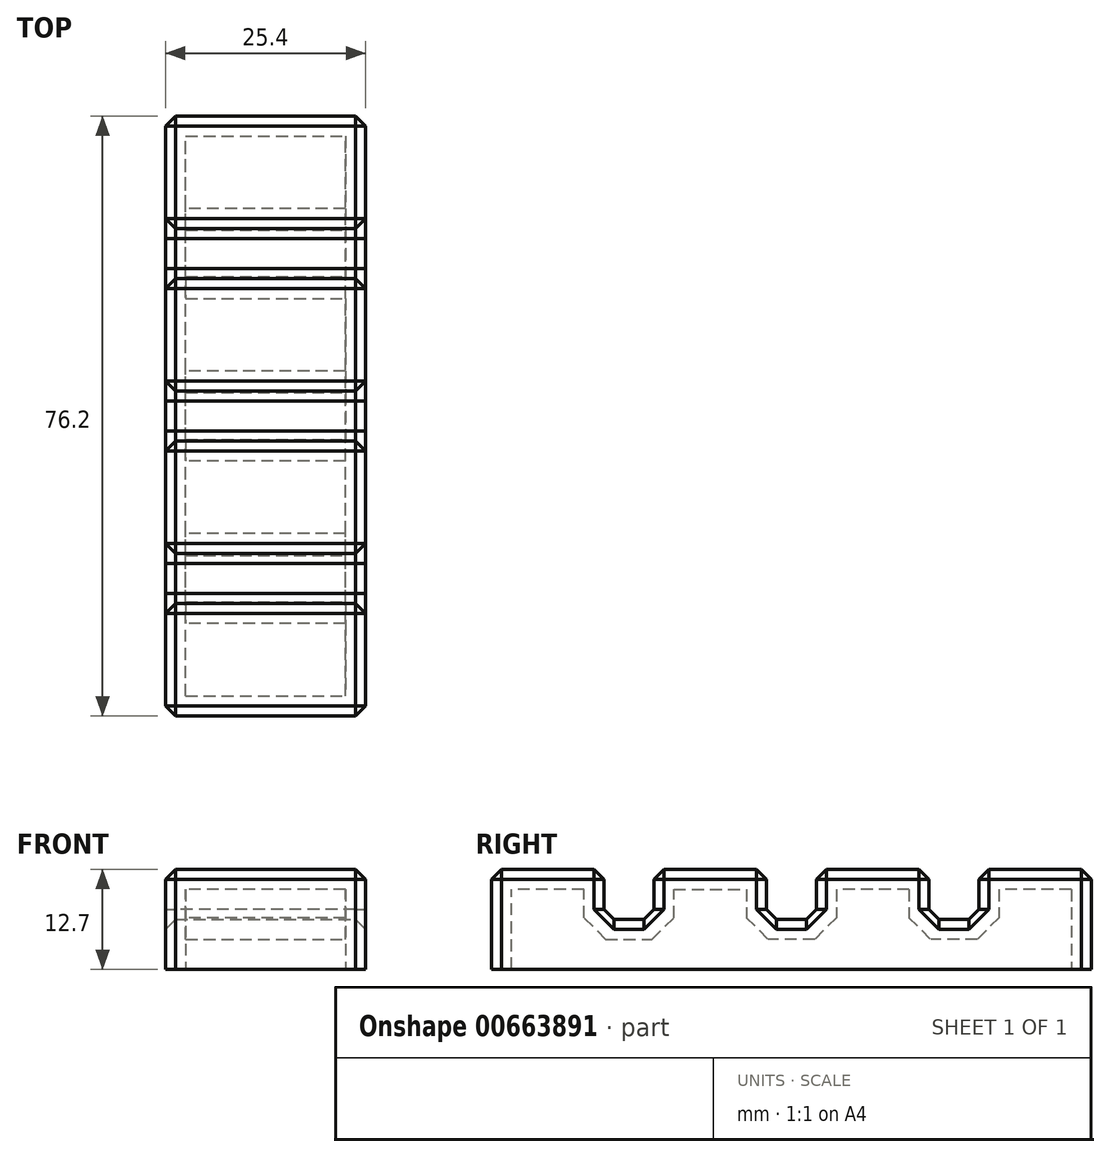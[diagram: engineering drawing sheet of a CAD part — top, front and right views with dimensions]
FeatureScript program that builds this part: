
annotation { "Feature Type Name" : "Feature", "Feature Type Description" : "" }
export const myFeature = defineFeature(function(context is Context, id is Id, definition is map)
    precondition{}
    {
        {
            var Q0;
            Q0=qCreatedBy(makeId("Top.planeOp"),FACE);
            var sketch = newSketch(context, id + "F0", { "sketchPlane" : qUnion([Q0])});
            skLineSegment(sketch, "E0.bottom", {"start": v(-12.7, -38.1) * mm, "end": v(12.7, -38.1) * mm});
            skLineSegment(sketch, "E0.top", {"start": v(-12.7, 38.1) * mm, "end": v(12.7, 38.1) * mm});
            skLineSegment(sketch, "E0.left", {"start": v(-12.7, -38.1) * mm, "end": v(-12.7, 38.1) * mm});
            skLineSegment(sketch, "E0.right", {"start": v(12.7, -38.1) * mm, "end": v(12.7, 38.1) * mm});
            skPoint(sketch, "E0.middle", {"position": v(0, 0) * mm});
            skSolve(sketch);
        }
        {
            var Q0;
            Q0 = qSketchRegion(id + "F0", true);
            extrude(context, id + "F1", {"entities" : qUnion([Q0]), "depth" : 12.7 * mm, "offsetDistance" : 25.4 * mm});
        }
        {
            var Q0;
            Q0=makeQuery(id+"F1.opExtrude","SWEPT_FACE",FACE,{"disambiguationData":[OSD([sQuery(id+"F0.wireOp",EDGE,"E0.left")])]});
            var sketch = newSketch(context, id + "F2", { "sketchPlane" : qUnion([Q0])});
            skLineSegment(sketch, "E1", {"start": v(-38.1, 6.35) * mm, "end": v(38.1, 6.35) * mm, "construction": true});
            skLineSegment(sketch, "E2.bottom", {"start": v(3.18, 6.35) * mm, "end": v(-3.17, 6.35) * mm});
            skLineSegment(sketch, "E2.top", {"start": v(3.18, 19.05) * mm, "end": v(-3.17, 19.05) * mm});
            skLineSegment(sketch, "E2.left", {"start": v(3.18, 6.35) * mm, "end": v(3.18, 19.05) * mm});
            skLineSegment(sketch, "E2.right", {"start": v(-3.17, 6.35) * mm, "end": v(-3.17, 19.05) * mm});
            skPoint(sketch, "E2.middle", {"position": v(0, 12.7) * mm});
            skLineSegment(sketch, "E3.bottom", {"start": v(23.83, 6.35) * mm, "end": v(17.48, 6.35) * mm});
            skLineSegment(sketch, "E3.top", {"start": v(23.83, 19.05) * mm, "end": v(17.48, 19.05) * mm});
            skLineSegment(sketch, "E3.left", {"start": v(23.83, 6.35) * mm, "end": v(23.83, 19.05) * mm});
            skLineSegment(sketch, "E3.right", {"start": v(17.48, 6.35) * mm, "end": v(17.48, 19.05) * mm});
            skPoint(sketch, "E3.middle", {"position": v(20.65, 12.7) * mm});
            skLineSegment(sketch, "E4.bottom", {"start": v(-17.48, 6.35) * mm, "end": v(-23.83, 6.35) * mm});
            skLineSegment(sketch, "E4.top", {"start": v(-17.48, 19.05) * mm, "end": v(-23.83, 19.05) * mm});
            skLineSegment(sketch, "E4.left", {"start": v(-17.48, 6.35) * mm, "end": v(-17.48, 19.05) * mm});
            skLineSegment(sketch, "E4.right", {"start": v(-23.83, 6.35) * mm, "end": v(-23.83, 19.05) * mm});
            skPoint(sketch, "E4.middle", {"position": v(-20.65, 12.7) * mm});
            skSolve(sketch);
        }
        {
            var Q0;
            {var subQ0=sQuery(id+"F2.wireOp",EDGE,"E4.bottom");Q0=makeQuery(id+"F2.imprint","IMPRINT",FACE,{"disambiguationData":[TD([[makeQuery(id+"F2.imprint","IMPRINT",EDGE,{"derivedFrom":subQ0}),-1.0]])]});}
            var Q1;
            {var subQ0=sQuery(id+"F2.wireOp",EDGE,"E4.top");Q1=makeQuery(id+"F2.imprint","IMPRINT",FACE,{"disambiguationData":[TD([[makeQuery(id+"F2.imprint","IMPRINT",EDGE,{"derivedFrom":subQ0}),1.0]])]});}
            var Q2;
            {var subQ0=sQuery(id+"F2.wireOp",EDGE,"E2.top");Q2=makeQuery(id+"F2.imprint","IMPRINT",FACE,{"disambiguationData":[TD([[makeQuery(id+"F2.imprint","IMPRINT",EDGE,{"derivedFrom":subQ0}),1.0]])]});}
            var Q3;
            {var subQ0=sQuery(id+"F2.wireOp",EDGE,"E2.bottom");Q3=makeQuery(id+"F2.imprint","IMPRINT",FACE,{"disambiguationData":[TD([[makeQuery(id+"F2.imprint","IMPRINT",EDGE,{"derivedFrom":subQ0}),-1.0]])]});}
            var Q4;
            {var subQ0=sQuery(id+"F2.wireOp",EDGE,"E3.bottom");Q4=makeQuery(id+"F2.imprint","IMPRINT",FACE,{"disambiguationData":[TD([[makeQuery(id+"F2.imprint","IMPRINT",EDGE,{"derivedFrom":subQ0}),-1.0]])]});}
            var Q5;
            {var subQ0=sQuery(id+"F2.wireOp",EDGE,"E3.top");Q5=makeQuery(id+"F2.imprint","IMPRINT",FACE,{"disambiguationData":[TD([[makeQuery(id+"F2.imprint","IMPRINT",EDGE,{"derivedFrom":subQ0}),1.0]])]});}
            var Q6;
            Q6 = qSketchRegion(id + "F2", true);
            extrude(context, id + "F3", {"entities" : qUnion([Q0, Q1, Q2, Q3, Q4, Q5, Q6]), "operationType" : NewBodyOperationType.REMOVE, "endBound" : BoundingType.THROUGH_ALL, "oppositeDirection" : true, "depth" : 25.4 * mm, "offsetDistance" : 25.4 * mm});
        }
        {
            var Q0;
            {var subQ0=sQuery(id+"F0.wireOp",EDGE,"E0.left");var subQ1=sQuery(id+"F0.wireOp",EDGE,"E0.right");Q0=makeQuery(id+"F3.boolean.opBoolean","SPLIT",FACE,{"disambiguationData":[TD([makeQuery(id+"F3.opExtrude","SWEPT_FACE",FACE,{"disambiguationData":[OSD([sQuery(id+"F2.wireOp",EDGE,"E2.left")])]})])],"derivedFrom":makeQuery(id+"F1.opExtrude","CAP_FACE",FACE,{"disambiguationData":[OSD([sQuery(id+"F0.wireOp",EDGE,"E0.bottom"),sQuery(id+"F0.wireOp",EDGE,"E0.top"),subQ0,subQ1])],"isStart":false})});}
            var Q1;
            {var subQ0=sQuery(id+"F0.wireOp",EDGE,"E0.top");var subQ1=sQuery(id+"F0.wireOp",EDGE,"E0.left");var subQ2=sQuery(id+"F0.wireOp",EDGE,"E0.right");Q1=makeQuery(id+"F3.boolean.opBoolean","SPLIT",FACE,{"disambiguationData":[TD([makeQuery(id+"F1.opExtrude","SWEPT_FACE",FACE,{"disambiguationData":[OSD([subQ0])]})])],"derivedFrom":makeQuery(id+"F1.opExtrude","CAP_FACE",FACE,{"disambiguationData":[OSD([sQuery(id+"F0.wireOp",EDGE,"E0.bottom"),subQ0,subQ1,subQ2])],"isStart":false})});}
            var Q2;
            Q2=makeQuery(id+"F3.boolean.opBoolean","COPY",FACE,{"derivedFrom":makeQuery(id+"F3.opExtrude","SWEPT_FACE",FACE,{"disambiguationData":[OSD([sQuery(id+"F2.wireOp",EDGE,"E2.bottom")])]})});
            var Q3;
            Q3=makeQuery(id+"F3.boolean.opBoolean","COPY",FACE,{"derivedFrom":makeQuery(id+"F3.opExtrude","SWEPT_FACE",FACE,{"disambiguationData":[OSD([sQuery(id+"F2.wireOp",EDGE,"E3.bottom")])]})});
            var Q4;
            Q4=makeQuery(id+"F3.boolean.opBoolean","COPY",FACE,{"derivedFrom":makeQuery(id+"F3.opExtrude","SWEPT_FACE",FACE,{"disambiguationData":[OSD([sQuery(id+"F2.wireOp",EDGE,"E4.bottom")])]})});
            var Q5;
            {var subQ0=sQuery(id+"F0.wireOp",EDGE,"E0.left");var subQ1=sQuery(id+"F0.wireOp",EDGE,"E0.right");Q5=makeQuery(id+"F3.boolean.opBoolean","SPLIT",FACE,{"disambiguationData":[TD([makeQuery(id+"F3.opExtrude","SWEPT_FACE",FACE,{"disambiguationData":[OSD([sQuery(id+"F2.wireOp",EDGE,"E2.right")])]})])],"derivedFrom":makeQuery(id+"F1.opExtrude","CAP_FACE",FACE,{"disambiguationData":[OSD([sQuery(id+"F0.wireOp",EDGE,"E0.bottom"),sQuery(id+"F0.wireOp",EDGE,"E0.top"),subQ0,subQ1])],"isStart":false})});}
            var Q6;
            {var subQ0=sQuery(id+"F0.wireOp",EDGE,"E0.bottom");var subQ1=sQuery(id+"F0.wireOp",EDGE,"E0.right");var subQ2=sQuery(id+"F0.wireOp",EDGE,"E0.left");Q6=makeQuery(id+"F3.boolean.opBoolean","SPLIT",FACE,{"disambiguationData":[TD([makeQuery(id+"F1.opExtrude","SWEPT_FACE",FACE,{"disambiguationData":[OSD([subQ0])]})])],"derivedFrom":makeQuery(id+"F1.opExtrude","CAP_FACE",FACE,{"disambiguationData":[OSD([subQ0,sQuery(id+"F0.wireOp",EDGE,"E0.top"),subQ2,subQ1])],"isStart":false})});}
            var Q7;
            Q7=makeQuery(id+"F1.opExtrude","SWEPT_EDGE",EDGE,{"disambiguationData":[OSD([sQuery(id+"F0.wireOp",EDGE,"E0.top"),sQuery(id+"F0.wireOp",EDGE,"E0.left")])]});
            var Q8;
            Q8=makeQuery(id+"F1.opExtrude","SWEPT_EDGE",EDGE,{"disambiguationData":[OSD([sQuery(id+"F0.wireOp",EDGE,"E0.top"),sQuery(id+"F0.wireOp",EDGE,"E0.right")])]});
            var Q9;
            Q9=makeQuery(id+"F1.opExtrude","SWEPT_EDGE",EDGE,{"disambiguationData":[OSD([sQuery(id+"F0.wireOp",EDGE,"E0.bottom"),sQuery(id+"F0.wireOp",EDGE,"E0.left")])]});
            var Q10;
            Q10=makeQuery(id+"F1.opExtrude","SWEPT_EDGE",EDGE,{"disambiguationData":[OSD([sQuery(id+"F0.wireOp",EDGE,"E0.bottom"),sQuery(id+"F0.wireOp",EDGE,"E0.right")])]});
            chamfer(context, id + "F4", {"entities" : qUnion([Q0, Q1, Q2, Q3, Q4, Q5, Q6, Q7, Q8, Q9, Q10]), "width" : 1.27 * mm, "tangentPropagation" : true});
        }
        {
            var Q0;
            Q0=makeQuery(id+"F1.opExtrude","CAP_FACE",FACE,{"disambiguationData":[OSD([sQuery(id+"F0.wireOp",EDGE,"E0.bottom"),sQuery(id+"F0.wireOp",EDGE,"E0.top"),sQuery(id+"F0.wireOp",EDGE,"E0.left"),sQuery(id+"F0.wireOp",EDGE,"E0.right")])],"isStart":true});
            shell(context, id + "F5", {"entities" : qUnion([Q0]), "thickness" : 2.54 * mm});
        }
    });
